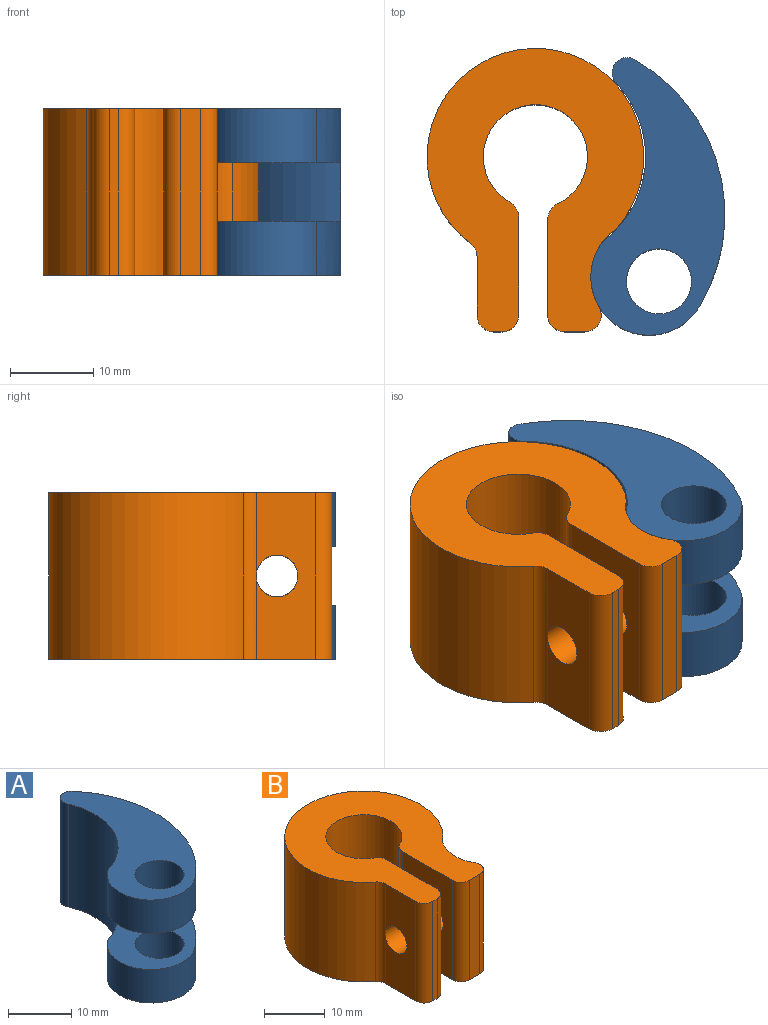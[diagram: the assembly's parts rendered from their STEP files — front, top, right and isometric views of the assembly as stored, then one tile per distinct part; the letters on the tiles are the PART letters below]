
ASSEMBLY  parts=2 mates=1
PART A: 12 faces, bbox 19.4x32.7x20 mm
  f0: cylinder r=12.76mm len=20mm, axis (0,0,-1), area 368.2mm2, adj f1,f4,f5,f6,f7,f9,f10,f11
  f1: cylinder r=7mm len=12.84mm, axis (0,0,-1), area 148.8mm2, adj f0,f2,f7,f10
  f2: cylinder r=21.38mm len=30.06mm, axis (0,0,-1), area 595.7mm2, adj f1,f4,f5,f6,f7,f9,f10,f11
  f3: cylinder r=3.9mm len=7.8mm, axis (0,0,1), area 159.3mm2, adj f7,f10
  f4: cylinder r=7mm len=12.84mm, axis (0,0,-1), area 148.8mm2, adj f0,f2,f6,f11
  f5: cylinder r=1.83mm len=20mm, axis (0,0,-1), area 115mm2, adj f0,f2,f6,f7
  f6: plane 32.72x19.42mm, normal (0,0,1), area 278.6mm2, adj f0,f2,f4,f5,f8
  f7: plane 32.72x19.42mm, normal (0,0,-1), area 278.6mm2, adj f0,f1,f2,f3,f5
  f8: cylinder r=3.9mm len=7.8mm, axis (0,0,1), area 159.3mm2, adj f6,f11
  f9: cylinder r=14.92mm len=7.69mm, axis (0,0,1), area 77.8mm2, adj f0,f2,f10,f11
  f10: plane 17.97x17.89mm, normal (0,0,1), area 146.5mm2, adj f0,f1,f2,f3,f9
  f11: plane 17.97x17.89mm, normal (0,0,-1), area 146.5mm2, adj f0,f2,f4,f8,f9
PART B: 19 faces, bbox 26x34x20 mm
  f0: cylinder r=7mm len=20mm, axis (0,0,-1), area 191.4mm2, adj f1,f14,f15,f16,f17
  f1: cylinder r=13mm len=26mm, axis (0,0,-1), area 1246.4mm2, adj f0,f2,f15,f16
  f2: cylinder r=2mm len=20mm, axis (0,0,-1), area 37mm2, adj f1,f3,f15,f16,f18
  f3: plane 20x7mm, normal (-1,0,0), area 120.4mm2, adj f2,f4,f15,f16,f18
  f4: cylinder r=2mm len=20mm, axis (0,0,-1), area 62.8mm2, adj f3,f5,f15,f16
  f5: plane 20x1mm, normal (0,-1,0), area 20mm2, adj f4,f6,f15,f16
  f6: cylinder r=2mm len=20mm, axis (0,0,-1), area 62.8mm2, adj f5,f7,f15,f16
  f7: plane 20x11.78mm, normal (1,0,0), area 216.1mm2, adj f6,f8,f15,f16,f18
  f8: cylinder r=2mm len=20mm, axis (0,0,-1), area 42.6mm2, adj f7,f9,f15,f16
  f9: cylinder r=6.25mm len=20mm, axis (0,0,-1), area 667.4mm2, adj f8,f10,f15,f16
  f10: cylinder r=2mm len=20mm, axis (0,0,-1), area 45.3mm2, adj f9,f11,f15,f16
  f11: plane 20x11.53mm, normal (-1,0,0), area 210.9mm2, adj f10,f12,f15,f16,f17
  f12: cylinder r=2mm len=20mm, axis (0,0,-1), area 62.8mm2, adj f11,f13,f15,f16
  f13: plane 20x2.4mm, normal (0,-1,0), area 48.1mm2, adj f12,f14,f15,f16
  f14: cylinder r=2mm len=20mm, axis (0,0,-1), area 84.2mm2, adj f0,f13,f15,f16
  f15: plane 34x26mm, normal (0,0,1), area 475.9mm2, adj f0,f1,f2,f3,f4,f5,f6,f7
  f16: plane 34x26mm, normal (0,0,-1), area 475.9mm2, adj f0,f1,f2,f3,f4,f5,f6,f7
  f17: cylinder r=2.5mm len=5.61mm, axis (-1,0,0), area 84.5mm2, adj f0,f11
  f18: cylinder r=2.5mm len=5mm, axis (-1,0,0), area 78.5mm2, adj f2,f3,f7
PLACE A rot(axis=(0,0,1),20.2deg) t=(5.39,-9.04,-3.77)mm
PLACE B t=(-8.26,5.38,-3.77)mm fixed
MATE revolute B.f0 <-> A.f1  axis (0,0,1) through (5.39,-9.04,16.23)mm
